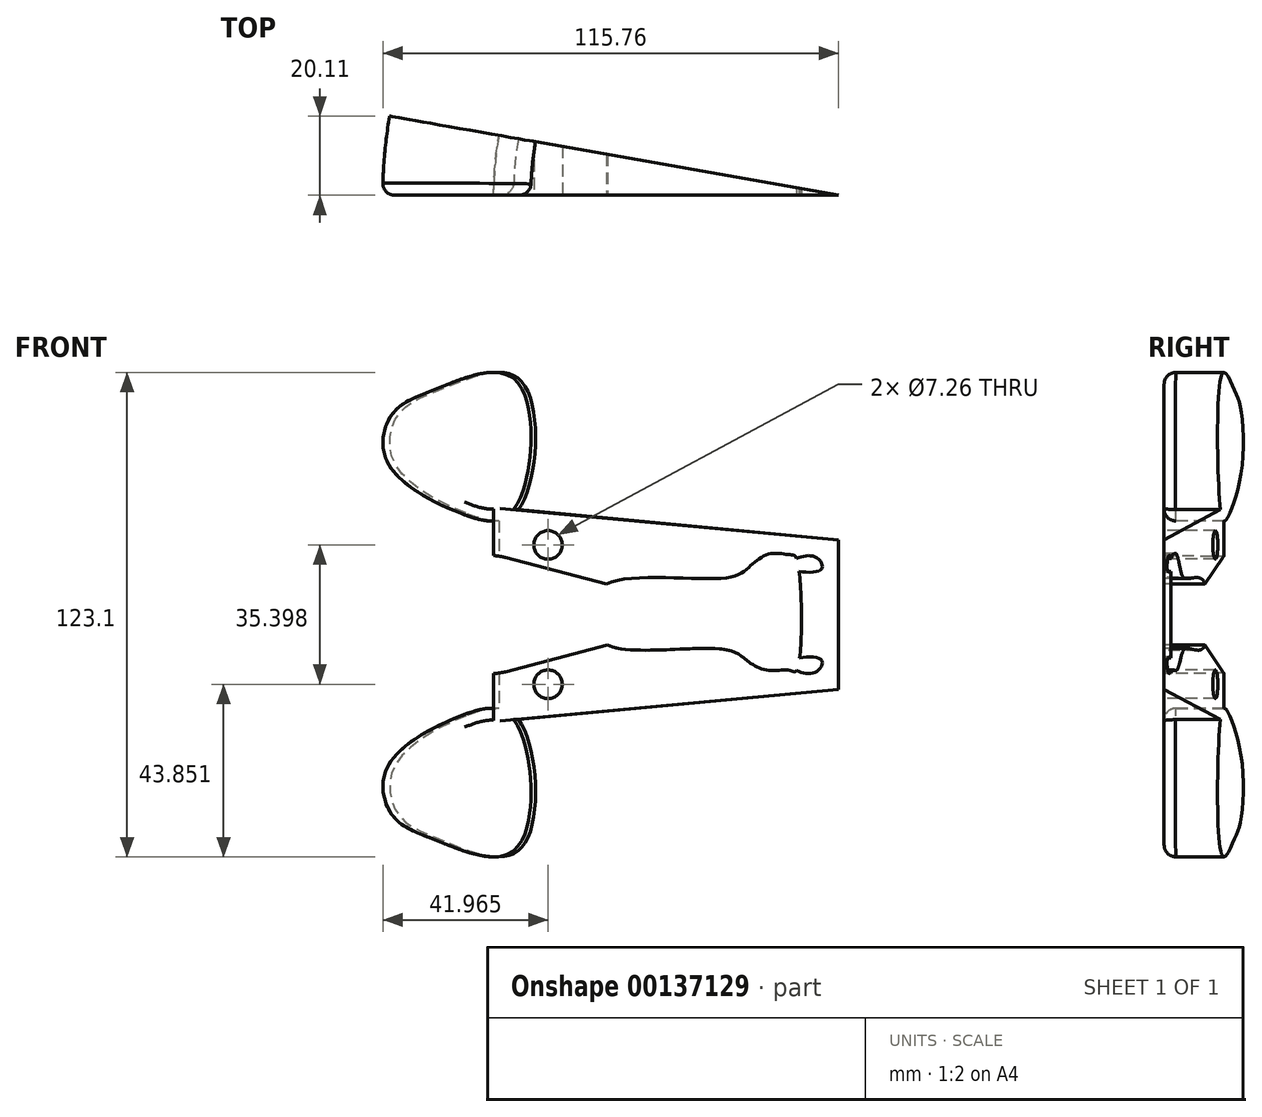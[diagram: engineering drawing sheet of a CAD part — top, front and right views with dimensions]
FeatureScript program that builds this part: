
annotation { "Feature Type Name" : "Feature", "Feature Type Description" : "" }
export const myFeature = defineFeature(function(context is Context, id is Id, definition is map)
    precondition{}
    {
        {
            var Q0;
            Q0=qCreatedBy(makeId("Front.planeOp"),FACE);
            var sketch = newSketch(context, id + "F0", { "sketchPlane" : qUnion([Q0])});
            skLineSegment(sketch, "E0", {"start": v(-57.8, 0) * mm, "end": v(57.2, 0) * mm});
            skCircle(sketch, "E1", {"center": v(-30.4, 0) * mm, "radius": 27.16 * mm});
            skLineSegment(sketch, "E2", {"start": v(-30.4, 0) * mm, "end": v(-30.4, 27.16) * mm});
            skLineSegment(sketch, "E3", {"start": v(-30.4, 27.16) * mm, "end": v(57.2, 19) * mm});
            skLineSegment(sketch, "E4.MirrorCS", {"start": v(-30.4, -27.16) * mm, "end": v(57.2, -19) * mm});
            skLineSegment(sketch, "E5.MirrorCS", {"start": v(-30.4, 0) * mm, "end": v(-30.4, -27.16) * mm});
            skFitSpline(sketch, "E6", {"points": [v(-38.93, 25.78) * mm, v(-57.48, 38.8) * mm, v(-56.27, 50.92) * mm, v(-44.96, 57.38) * mm, v(-24.75, 59.4) * mm, v(-25.4, 26.69) * mm, v(-38.93, 25.78) * mm]});
            skFitSpline(sketch, "E7.MirrorC", {"points": [v(-38.93, -25.78) * mm, v(-57.48, -38.8) * mm, v(-56.27, -50.92) * mm, v(-44.96, -57.38) * mm, v(-24.75, -59.4) * mm, v(-25.4, -26.69) * mm, v(-38.93, -25.78) * mm]});
            skLineSegment(sketch, "E8", {"start": v(57.2, 19) * mm, "end": v(57.2, -19) * mm});
            skSolve(sketch);
        }
        {
            var Q0;
            {var subQ0=sQuery(id+"F0.wireOp",EDGE,"E8");var subQ1=sQuery(id+"F0.wireOp",EDGE,"E0");var subQ2=makeQuery(id+"F0.imprint","INTERSECT",VERTEX,{"derivedFrom":[subQ1,subQ0]});Q0=makeQuery(id+"F0.imprint","IMPRINT",FACE,{"disambiguationData":[TD([[makeQuery(id+"F0.imprint","IMPRINT",EDGE,{"disambiguationData":[TD([[subQ2,1.0]])],"derivedFrom":subQ1}),1.0]])]});}
            var Q1;
            {var subQ0=sQuery(id+"F0.wireOp",EDGE,"E8");var subQ1=sQuery(id+"F0.wireOp",EDGE,"E0");var subQ2=makeQuery(id+"F0.imprint","INTERSECT",VERTEX,{"derivedFrom":[subQ1,subQ0]});Q1=makeQuery(id+"F0.imprint","IMPRINT",FACE,{"disambiguationData":[TD([[makeQuery(id+"F0.imprint","IMPRINT",EDGE,{"disambiguationData":[TD([[subQ2,1.0]])],"derivedFrom":subQ1}),-1.0]])]});}
            var Q2;
            {var subQ1=sQuery(id+"F0.wireOp",EDGE,"E1");var subQ3=sQuery(id+"F0.wireOp",EDGE,"E6");var subQ5=makeQuery(id+"F0.imprint","INTERSECT",VERTEX,{"derivedFrom":[subQ1,subQ3]});Q2=makeQuery(id+"F0.imprint","IMPRINT",FACE,{"disambiguationData":[TD([[makeQuery(id+"F0.imprint","IMPRINT",EDGE,{"disambiguationData":[TD([[subQ5,1.0]])],"derivedFrom":subQ1}),-1.0]])]});}
            var Q3;
            {var subQ0=sQuery(id+"F0.wireOp",EDGE,"E3");var subQ1=sQuery(id+"F0.wireOp",EDGE,"E1");var subQ2=makeQuery(id+"F0.imprint","INTERSECT",VERTEX,{"derivedFrom":[subQ1,sQuery(id+"F0.wireOp",EDGE,"E2"),subQ0]});Q3=makeQuery(id+"F0.imprint","IMPRINT",FACE,{"disambiguationData":[TD([[makeQuery(id+"F0.imprint","IMPRINT",EDGE,{"disambiguationData":[TD([[subQ2,1.0]])],"derivedFrom":subQ1}),1.0]])]});}
            var Q4;
            {var subQ1=sQuery(id+"F0.wireOp",EDGE,"E1");var subQ3=sQuery(id+"F0.wireOp",EDGE,"E7.MirrorC");var subQ4=makeQuery(id+"F0.imprint","INTERSECT",VERTEX,{"derivedFrom":[subQ1,subQ3]});Q4=makeQuery(id+"F0.imprint","IMPRINT",FACE,{"disambiguationData":[TD([[makeQuery(id+"F0.imprint","IMPRINT",EDGE,{"disambiguationData":[TD([[subQ4,-1.0]])],"derivedFrom":subQ1}),-1.0]])]});}
            var Q5;
            {var subQ0=sQuery(id+"F0.wireOp",EDGE,"E4.MirrorCS");var subQ1=sQuery(id+"F0.wireOp",EDGE,"E1");var subQ2=makeQuery(id+"F0.imprint","INTERSECT",VERTEX,{"derivedFrom":[subQ1,subQ0,sQuery(id+"F0.wireOp",EDGE,"E5.MirrorCS")]});Q5=makeQuery(id+"F0.imprint","IMPRINT",FACE,{"disambiguationData":[TD([[makeQuery(id+"F0.imprint","IMPRINT",EDGE,{"disambiguationData":[TD([[subQ2,-1.0]])],"derivedFrom":subQ1}),1.0]])]});}
            var Q6;
            {var subQ1=sQuery(id+"F0.wireOp",EDGE,"E0");var subQ3=sQuery(id+"F0.wireOp",EDGE,"E1");var subQ4=makeQuery(id+"F0.imprint","INTERSECT",VERTEX,{"disambiguationData":[OD(0.0)],"derivedFrom":[subQ1,subQ3]});Q6=makeQuery(id+"F0.imprint","IMPRINT",FACE,{"disambiguationData":[TD([[makeQuery(id+"F0.imprint","IMPRINT",EDGE,{"disambiguationData":[TD([[subQ4,1.0]])],"derivedFrom":subQ3}),1.0]])]});}
            var Q7;
            {var subQ1=sQuery(id+"F0.wireOp",EDGE,"E0");var subQ3=sQuery(id+"F0.wireOp",EDGE,"E1");var subQ4=makeQuery(id+"F0.imprint","INTERSECT",VERTEX,{"disambiguationData":[OD(0.0)],"derivedFrom":[subQ1,subQ3]});Q7=makeQuery(id+"F0.imprint","IMPRINT",FACE,{"disambiguationData":[TD([[makeQuery(id+"F0.imprint","IMPRINT",EDGE,{"disambiguationData":[TD([[subQ4,-1.0]])],"derivedFrom":subQ3}),1.0]])]});}
            var Q8;
            {var subQ1=sQuery(id+"F0.wireOp",EDGE,"E1");var subQ3=sQuery(id+"F0.wireOp",EDGE,"E7.MirrorC");var subQ4=makeQuery(id+"F0.imprint","INTERSECT",VERTEX,{"derivedFrom":[subQ1,subQ3]});Q8=makeQuery(id+"F0.imprint","IMPRINT",FACE,{"disambiguationData":[TD([[makeQuery(id+"F0.imprint","IMPRINT",EDGE,{"disambiguationData":[TD([[subQ4,1.0]])],"derivedFrom":subQ3}),1.0]])]});}
            var Q9;
            {var subQ0=sQuery(id+"F0.wireOp",EDGE,"E5.MirrorCS");var subQ4=sQuery(id+"F0.wireOp",EDGE,"E7.MirrorC");var subQ6=makeQuery(id+"F0.imprint","INTERSECT",VERTEX,{"derivedFrom":[subQ0,subQ4]});Q9=makeQuery(id+"F0.imprint","IMPRINT",FACE,{"disambiguationData":[TD([[makeQuery(id+"F0.imprint","IMPRINT",EDGE,{"disambiguationData":[TD([[subQ6,-1.0]])],"derivedFrom":subQ0}),1.0]])]});}
            var Q10;
            {var subQ1=sQuery(id+"F0.wireOp",EDGE,"E0");var subQ3=sQuery(id+"F0.wireOp",EDGE,"E1");var subQ4=makeQuery(id+"F0.imprint","INTERSECT",VERTEX,{"disambiguationData":[OD(1.0)],"derivedFrom":[subQ1,subQ3]});Q10=makeQuery(id+"F0.imprint","IMPRINT",FACE,{"disambiguationData":[TD([[makeQuery(id+"F0.imprint","IMPRINT",EDGE,{"disambiguationData":[TD([[subQ4,1.0]])],"derivedFrom":subQ1}),1.0]])]});}
            var Q11;
            {var subQ1=sQuery(id+"F0.wireOp",EDGE,"E0");var subQ3=sQuery(id+"F0.wireOp",EDGE,"E1");var subQ4=makeQuery(id+"F0.imprint","INTERSECT",VERTEX,{"disambiguationData":[OD(1.0)],"derivedFrom":[subQ1,subQ3]});Q11=makeQuery(id+"F0.imprint","IMPRINT",FACE,{"disambiguationData":[TD([[makeQuery(id+"F0.imprint","IMPRINT",EDGE,{"disambiguationData":[TD([[subQ4,1.0]])],"derivedFrom":subQ1}),-1.0]])]});}
            var Q12;
            {var subQ1=sQuery(id+"F0.wireOp",EDGE,"E1");var subQ3=sQuery(id+"F0.wireOp",EDGE,"E6");var subQ4=makeQuery(id+"F0.imprint","INTERSECT",VERTEX,{"derivedFrom":[subQ1,subQ3]});Q12=makeQuery(id+"F0.imprint","IMPRINT",FACE,{"disambiguationData":[TD([[makeQuery(id+"F0.imprint","IMPRINT",EDGE,{"disambiguationData":[TD([[subQ4,1.0]])],"derivedFrom":subQ3}),-1.0]])]});}
            var Q13;
            {var subQ1=sQuery(id+"F0.wireOp",EDGE,"E2");var subQ4=sQuery(id+"F0.wireOp",EDGE,"E6");var subQ5=makeQuery(id+"F0.imprint","INTERSECT",VERTEX,{"derivedFrom":[subQ1,subQ4]});Q13=makeQuery(id+"F0.imprint","IMPRINT",FACE,{"disambiguationData":[TD([[makeQuery(id+"F0.imprint","IMPRINT",EDGE,{"disambiguationData":[TD([[subQ5,-1.0]])],"derivedFrom":subQ1}),-1.0]])]});}
            var Q14;
            Q14=sQuery(id+"F0.wireOp",EDGE,"E8");
            revolve(context, id + "F1", {"entities" : qUnion([Q0, Q1, Q2, Q3, Q4, Q5, Q6, Q7, Q8, Q9, Q10, Q11, Q12, Q13]), "axis" : qUnion([Q14]), "revolveType" : RevolveType.ONE_DIRECTION, "angle" : 10 * degree});
        }
        {
            var Q0;
            Q0=makeQuery(id+"F1.opRevolve","CAP_FACE",FACE,{"disambiguationData":[OSD([sQuery(id+"F0.wireOp",EDGE,"E1"),sQuery(id+"F0.wireOp",EDGE,"E3"),sQuery(id+"F0.wireOp",EDGE,"E4.MirrorCS"),sQuery(id+"F0.wireOp",EDGE,"E6"),sQuery(id+"F0.wireOp",EDGE,"E7.MirrorC"),sQuery(id+"F0.wireOp",EDGE,"E8")])],"isStart":true});
            var sketch = newSketch(context, id + "F2", { "sketchPlane" : qUnion([Q0])});
            skCircle(sketch, "E9", {"center": v(-31.22, 0) * mm, "radius": 15 * mm});
            skLineSegment(sketch, "E10", {"start": v(-27.42, -14.51) * mm, "end": v(28.05, 0) * mm});
            skLineSegment(sketch, "E11.MirrorCS", {"start": v(-27.42, 14.51) * mm, "end": v(28.05, 0) * mm});
            skFitSpline(sketch, "E12", {"points": [v(44.73, -12.01) * mm, v(46.52, -14.2) * mm, v(51.69, -14.4) * mm, v(52.68, -11.42) * mm, v(44.73, -12.01) * mm]});
            skFitSpline(sketch, "E13.MirrorC", {"points": [v(44.73, 12.01) * mm, v(46.52, 14.2) * mm, v(51.69, 14.4) * mm, v(52.68, 11.42) * mm, v(44.73, 12.01) * mm]});
            skLineSegment(sketch, "E14.bottom", {"start": v(44.73, -12.01) * mm, "end": v(34.39, -12.01) * mm});
            skLineSegment(sketch, "E14.top", {"start": v(44.73, 12.01) * mm, "end": v(34.39, 12.01) * mm});
            skLineSegment(sketch, "E14.left", {"start": v(44.73, -12.01) * mm, "end": v(44.73, 12.01) * mm});
            skLineSegment(sketch, "E14.right", {"start": v(34.39, -12.01) * mm, "end": v(34.39, 12.01) * mm});
            skPoint(sketch, "E14.middle", {"position": v(39.56, 0) * mm});
            skPoint(sketch, "E15.2.internal.snap0", {"position": v(39.56, -12.01) * mm});
            skPoint(sketch, "E15.6.internal.snap0", {"position": v(44.73, 0) * mm});
            skPoint(sketch, "E15.10.internal.snap0", {"position": v(39.56, -12.01) * mm});
            skFitSpline(sketch, "E15", {"points": [v(46.52, -14.2) * mm, v(44.73, -14.2) * mm, v(39.56, -14.2) * mm, v(34.39, -12.01) * mm, v(28.05, -8.83) * mm, v(-1.55, -7.74) * mm, v(-4.99, 0) * mm, v(-1.76, 7.8) * mm, v(28.05, 9.26) * mm, v(34.39, 12.01) * mm, v(39.56, 15.43) * mm, v(44.73, 15.23) * mm, v(46.52, 14.2) * mm, v(46.52, -14.2) * mm]});
            skSolve(sketch);
        }
        {
            var Q0;
            {var subQ0=sQuery(id+"F2.wireOp",EDGE,"E11.MirrorCS");var subQ1=sQuery(id+"F2.wireOp",EDGE,"E10");var subQ2=makeQuery(id+"F2.imprint","INTERSECT",VERTEX,{"derivedFrom":[subQ1,subQ0]});Q0=makeQuery(id+"F2.imprint","IMPRINT",FACE,{"disambiguationData":[TD([[makeQuery(id+"F2.imprint","IMPRINT",EDGE,{"disambiguationData":[TD([[subQ2,1.0]])],"derivedFrom":subQ1}),1.0]])]});}
            var Q1;
            {var subQ0=sQuery(id+"F2.wireOp",EDGE,"E15");var subQ1=sQuery(id+"F2.wireOp",EDGE,"E12");var subQ2=makeQuery(id+"F2.imprint","INTERSECT",VERTEX,{"disambiguationData":[OD(0.0)],"derivedFrom":[subQ1,subQ0]});Q1=makeQuery(id+"F2.imprint","IMPRINT",FACE,{"disambiguationData":[TD([[makeQuery(id+"F2.imprint","IMPRINT",EDGE,{"disambiguationData":[TD([[subQ2,-1.0]])],"derivedFrom":subQ1}),1.0]])]});}
            var Q2;
            {var subQ0=sQuery(id+"F2.wireOp",EDGE,"E15");var subQ1=sQuery(id+"F2.wireOp",EDGE,"E13.MirrorC");var subQ2=makeQuery(id+"F2.imprint","INTERSECT",VERTEX,{"disambiguationData":[OD(0.0)],"derivedFrom":[subQ1,subQ0]});Q2=makeQuery(id+"F2.imprint","IMPRINT",FACE,{"disambiguationData":[TD([[makeQuery(id+"F2.imprint","IMPRINT",EDGE,{"disambiguationData":[TD([[subQ2,-1.0]])],"derivedFrom":subQ1}),-1.0]])]});}
            var Q3;
            {var subQ0=sQuery(id+"F2.wireOp",EDGE,"E10");var subQ1=sQuery(id+"F2.wireOp",EDGE,"E9");var subQ2=makeQuery(id+"F2.imprint","INTERSECT",VERTEX,{"derivedFrom":[subQ1,subQ0]});Q3=makeQuery(id+"F2.imprint","IMPRINT",FACE,{"disambiguationData":[TD([[makeQuery(id+"F2.imprint","IMPRINT",EDGE,{"disambiguationData":[TD([[subQ2,-1.0]])],"derivedFrom":subQ1}),-1.0]])]});}
            var Q4;
            {var subQ1=sQuery(id+"F2.wireOp",EDGE,"E14.right");Q4=makeQuery(id+"F2.imprint","IMPRINT",FACE,{"disambiguationData":[TD([[makeQuery(id+"F2.imprint","IMPRINT",EDGE,{"derivedFrom":subQ1}),1.0]])]});}
            var Q5;
            {var subQ0=sQuery(id+"F2.wireOp",EDGE,"E12");var subQ2=sQuery(id+"F2.wireOp",EDGE,"E15");var subQ3=makeQuery(id+"F2.imprint","INTERSECT",VERTEX,{"disambiguationData":[OD(0.0)],"derivedFrom":[subQ0,subQ2]});Q5=makeQuery(id+"F2.imprint","IMPRINT",FACE,{"disambiguationData":[TD([[makeQuery(id+"F2.imprint","IMPRINT",EDGE,{"disambiguationData":[TD([[subQ3,1.0]])],"derivedFrom":subQ2}),-1.0]])]});}
            var Q6;
            {var subQ0=sQuery(id+"F2.wireOp",EDGE,"E14.bottom");Q6=makeQuery(id+"F2.imprint","IMPRINT",FACE,{"disambiguationData":[TD([[makeQuery(id+"F2.imprint","IMPRINT",EDGE,{"derivedFrom":subQ0}),1.0]])]});}
            var Q7;
            {var subQ0=sQuery(id+"F2.wireOp",EDGE,"E13.MirrorC");var subQ2=sQuery(id+"F2.wireOp",EDGE,"E15");var subQ3=makeQuery(id+"F2.imprint","INTERSECT",VERTEX,{"disambiguationData":[OD(0.0)],"derivedFrom":[subQ0,subQ2]});Q7=makeQuery(id+"F2.imprint","IMPRINT",FACE,{"disambiguationData":[TD([[makeQuery(id+"F2.imprint","IMPRINT",EDGE,{"disambiguationData":[TD([[subQ3,-1.0]])],"derivedFrom":subQ2}),-1.0]])]});}
            var Q8;
            {var subQ0=sQuery(id+"F2.wireOp",EDGE,"E14.top");Q8=makeQuery(id+"F2.imprint","IMPRINT",FACE,{"disambiguationData":[TD([[makeQuery(id+"F2.imprint","IMPRINT",EDGE,{"derivedFrom":subQ0}),-1.0]])]});}
            var Q9;
            {var subQ0=sQuery(id+"F2.wireOp",EDGE,"E14.left");Q9=makeQuery(id+"F2.imprint","IMPRINT",FACE,{"disambiguationData":[TD([[makeQuery(id+"F2.imprint","IMPRINT",EDGE,{"derivedFrom":subQ0}),-1.0]])]});}
            var Q10;
            Q10=makeQuery(id+"F2.imprint","IMPRINT",FACE,{"disambiguationData":[TD([[makeQuery(id+"F2.imprint","IMPRINT",EDGE,{"derivedFrom":sQuery(id+"F2.wireOp",EDGE,"E14.bottom")}),-1.0]])]});
            var Q11;
            {var subQ0=sQuery(id+"F2.wireOp",EDGE,"E9");var subQ1=makeQuery(id+"F2.imprint","INTERSECT",VERTEX,{"derivedFrom":[subQ0,sQuery(id+"F2.wireOp",EDGE,"E10")]});Q11=makeQuery(id+"F2.imprint","IMPRINT",FACE,{"disambiguationData":[TD([[makeQuery(id+"F2.imprint","IMPRINT",EDGE,{"disambiguationData":[TD([[subQ1,1.0]])],"derivedFrom":subQ0}),1.0]])]});}
            extrude(context, id + "F3", {"entities" : qUnion([Q0, Q1, Q2, Q3, Q4, Q5, Q6, Q7, Q8, Q9, Q10, Q11]), "operationType" : NewBodyOperationType.REMOVE, "oppositeDirection" : true, "depth" : 25 * mm});
        }
        {
            var Q0;
            Q0=makeQuery(id+"F1.opRevolve","CAP_FACE",FACE,{"disambiguationData":[OSD([sQuery(id+"F0.wireOp",EDGE,"E1"),sQuery(id+"F0.wireOp",EDGE,"E3"),sQuery(id+"F0.wireOp",EDGE,"E4.MirrorCS"),sQuery(id+"F0.wireOp",EDGE,"E6"),sQuery(id+"F0.wireOp",EDGE,"E7.MirrorC"),sQuery(id+"F0.wireOp",EDGE,"E8")])],"isStart":true});
            var sketch = newSketch(context, id + "F4", { "sketchPlane" : qUnion([Q0])});
            skCircle(sketch, "E16", {"center": v(-16.6, -17.7) * mm, "radius": 3.63 * mm});
            skCircle(sketch, "E17.MirrorC", {"center": v(-16.6, 17.7) * mm, "radius": 3.63 * mm});
            skSolve(sketch);
        }
        {
            var Q0;
            Q0 = qSketchRegion(id + "F4", true);
            extrude(context, id + "F5", {"entities" : qUnion([Q0]), "operationType" : NewBodyOperationType.REMOVE, "oppositeDirection" : true, "depth" : 25 * mm});
        }
        {
            var Q0;
            Q0=makeQuery(id+"F1.opRevolve","CAP_EDGE",EDGE,{"disambiguationData":[OSD([sQuery(id+"F0.wireOp",EDGE,"E6")])],"isStart":true});
            var Q1;
            Q1=makeQuery(id+"F1.opRevolve","CAP_EDGE",EDGE,{"disambiguationData":[OSD([sQuery(id+"F0.wireOp",EDGE,"E7.MirrorC")])],"isStart":true});
            var Q2;
            Q2=makeQuery(id+"F3.boolean.opBoolean","COPY",EDGE,{"derivedFrom":makeQuery(id+"F3.opExtrude","CAP_EDGE",EDGE,{"disambiguationData":[OSD([sQuery(id+"F2.wireOp",EDGE,"E9")])],"isStart":true})});
            var Q3;
            {var subQ0=sQuery(id+"F2.wireOp",EDGE,"E15");Q3=makeQuery(id+"F3.boolean.opBoolean","COPY",EDGE,{"derivedFrom":makeQuery(id+"F3.opExtrude","CAP_EDGE",EDGE,{"disambiguationData":[OSD([subQ0]),TDD([makeQuery(id+"F2.imprint","IMPRINT",EDGE,{"disambiguationData":[TD([[makeQuery(id+"F2.imprint","INTERSECT",VERTEX,{"derivedFrom":[sQuery(id+"F2.wireOp",EDGE,"E11.MirrorCS"),subQ0]}),-1.0]])],"derivedFrom":subQ0}),makeQuery(id+"F2.imprint","IMPRINT",EDGE,{"disambiguationData":[TD([[makeQuery(id+"F2.imprint","INTERSECT",VERTEX,{"disambiguationData":[OD(0.0)],"derivedFrom":[sQuery(id+"F2.wireOp",EDGE,"E13.MirrorC"),subQ0]}),1.0]])],"derivedFrom":subQ0})])],"isStart":true})});}
            var Q4;
            {var subQ0=sQuery(id+"F2.wireOp",EDGE,"E15");Q4=makeQuery(id+"F3.boolean.opBoolean","COPY",EDGE,{"derivedFrom":makeQuery(id+"F3.opExtrude","CAP_EDGE",EDGE,{"disambiguationData":[OSD([subQ0]),TDD([makeQuery(id+"F2.imprint","IMPRINT",EDGE,{"disambiguationData":[TD([[makeQuery(id+"F2.imprint","INTERSECT",VERTEX,{"disambiguationData":[OD(0.0)],"derivedFrom":[sQuery(id+"F2.wireOp",EDGE,"E12"),subQ0]}),-1.0]])],"derivedFrom":subQ0}),makeQuery(id+"F2.imprint","IMPRINT",EDGE,{"disambiguationData":[TD([[makeQuery(id+"F2.imprint","INTERSECT",VERTEX,{"derivedFrom":[sQuery(id+"F2.wireOp",EDGE,"E10"),subQ0]}),1.0]])],"derivedFrom":subQ0})])],"isStart":true})});}
            var Q5;
            Q5=makeQuery(id+"F3.boolean.opBoolean","COPY",EDGE,{"derivedFrom":makeQuery(id+"F3.opExtrude","CAP_EDGE",EDGE,{"disambiguationData":[OSD([sQuery(id+"F2.wireOp",EDGE,"E12")])],"isStart":true})});
            var Q6;
            {var subQ0=sQuery(id+"F2.wireOp",EDGE,"E15");Q6=makeQuery(id+"F3.boolean.opBoolean","COPY",EDGE,{"derivedFrom":makeQuery(id+"F3.opExtrude","CAP_EDGE",EDGE,{"disambiguationData":[OSD([subQ0]),TDD([makeQuery(id+"F2.imprint","IMPRINT",EDGE,{"disambiguationData":[TD([[makeQuery(id+"F2.imprint","INTERSECT",VERTEX,{"disambiguationData":[OD(1.0)],"derivedFrom":[sQuery(id+"F2.wireOp",EDGE,"E12"),subQ0]}),1.0]])],"derivedFrom":subQ0})])],"isStart":true})});}
            var Q7;
            Q7=makeQuery(id+"F3.boolean.opBoolean","COPY",EDGE,{"derivedFrom":makeQuery(id+"F3.opExtrude","CAP_EDGE",EDGE,{"disambiguationData":[OSD([sQuery(id+"F2.wireOp",EDGE,"E13.MirrorC")])],"isStart":true})});
            fillet(context, id + "F6", {"entities" : qUnion([Q0, Q1, Q2, Q3, Q4, Q5, Q6, Q7]), "radius" : 3 * mm, "tangentPropagation" : true, "allowEdgeOverflow" : false});
        }
    });
